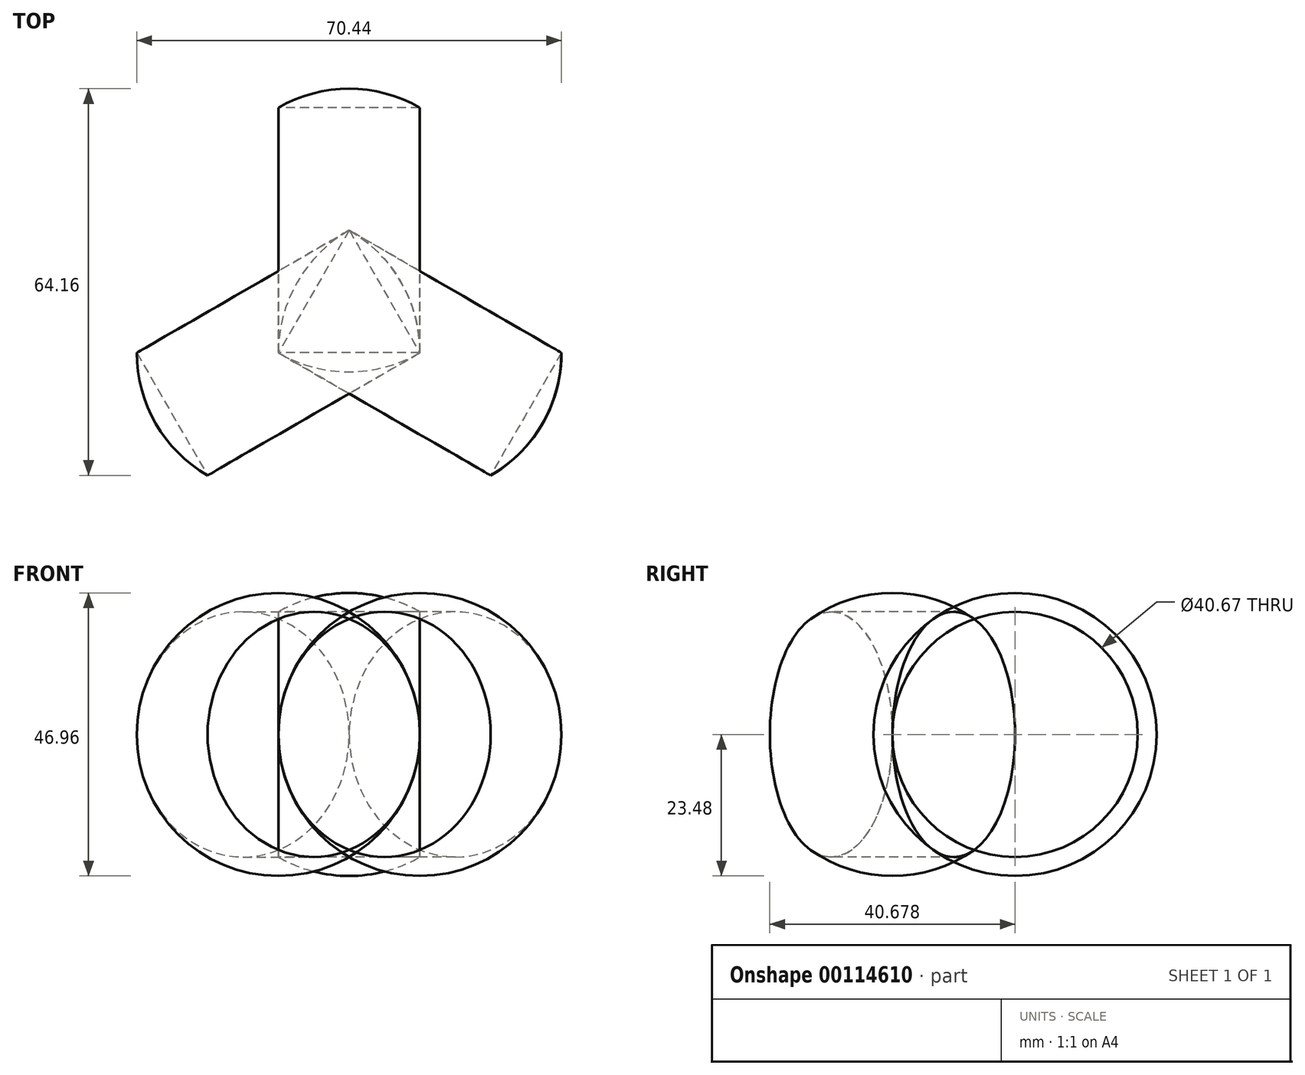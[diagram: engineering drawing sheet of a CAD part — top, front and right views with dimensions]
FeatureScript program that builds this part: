
annotation { "Feature Type Name" : "Feature", "Feature Type Description" : "" }
export const myFeature = defineFeature(function(context is Context, id is Id, definition is map)
    precondition{}
    {
        {
            var Q0;
            Q0=qCreatedBy(makeId("Top.planeOp"),FACE);
            var sketch = newSketch(context, id + "F0", { "sketchPlane" : qUnion([Q0])});
            skLineSegment(sketch, "E0", {"start": v(0, 13.56) * mm, "end": v(-11.74, -6.78) * mm});
            skLineSegment(sketch, "E1", {"start": v(-11.74, -6.78) * mm, "end": v(11.74, -6.78) * mm});
            skLineSegment(sketch, "E2", {"start": v(11.74, -6.78) * mm, "end": v(0, 13.56) * mm});
            skLineSegment(sketch, "E3", {"start": v(-11.74, -6.78) * mm, "end": v(5.87, 3.39) * mm, "construction": true});
            skLineSegment(sketch, "E4", {"start": v(-5.87, 3.39) * mm, "end": v(11.74, -6.78) * mm, "construction": true});
            skArc(sketch, "E5", {"start": v(-23.48, 13.56) * mm, "mid": v(-32.08, -18.52) * mm, "end": v(0, -27.12) * mm});
            skArc(sketch, "E6", {"start": v(0, 13.56) * mm, "mid": v(-8.6, 4.96) * mm, "end": v(-11.74, -6.78) * mm});
            skArc(sketch, "E7", {"start": v(-11.74, -6.78) * mm, "mid": v(0, -9.93) * mm, "end": v(11.74, -6.78) * mm});
            skArc(sketch, "E8.trimOffspring", {"start": v(11.74, -6.78) * mm, "mid": v(8.6, 4.96) * mm, "end": v(0, 13.56) * mm});
            skArc(sketch, "E9.trimOffspring", {"start": v(0, -27.12) * mm, "mid": v(32.08, -18.52) * mm, "end": v(23.48, 13.56) * mm});
            skArc(sketch, "E10.trimOffspring", {"start": v(23.48, 13.56) * mm, "mid": v(0, 37.04) * mm, "end": v(-23.48, 13.56) * mm});
            skLineSegment(sketch, "E11", {"start": v(-12.12, 13.56) * mm, "end": v(10.87, 13.56) * mm, "construction": true});
            skLineSegment(sketch, "E12", {"start": v(-11.74, -6.78) * mm, "end": v(-18.52, 4.96) * mm, "construction": true});
            skPoint(sketch, "E12.endSnap0", {"position": v(-8.6, 4.96) * mm});
            skLineSegment(sketch, "E13", {"start": v(11.74, -6.78) * mm, "end": v(19, 5.78) * mm, "construction": true});
            skSolve(sketch);
        }
        {
            var Q0;
            Q0=makeQuery(id+"F0.imprint","IMPRINT",FACE,{"disambiguationData":[TD([[makeQuery(id+"F0.imprint","IMPRINT",EDGE,{"derivedFrom":sQuery(id+"F0.wireOp",EDGE,"E1")}),-1.0]])]});
            var Q1;
            Q1=sQuery(id+"F0.wireOp",EDGE,"E11");
            revolve(context, id + "F1", {"entities" : qUnion([Q0]), "axis" : qUnion([Q1]), "revolveType" : RevolveType.FULL});
        }
        {
            var Q0;
            Q0=makeQuery(id+"F0.imprint","IMPRINT",FACE,{"disambiguationData":[TD([[makeQuery(id+"F0.imprint","IMPRINT",EDGE,{"derivedFrom":sQuery(id+"F0.wireOp",EDGE,"E0")}),-1.0]])]});
            var Q1;
            Q1=sQuery(id+"F0.wireOp",EDGE,"E13");
            revolve(context, id + "F2", {"entities" : qUnion([Q0]), "axis" : qUnion([Q1]), "revolveType" : RevolveType.FULL});
        }
        {
            var Q0;
            Q0=makeQuery(id+"F0.imprint","IMPRINT",FACE,{"disambiguationData":[TD([[makeQuery(id+"F0.imprint","IMPRINT",EDGE,{"derivedFrom":sQuery(id+"F0.wireOp",EDGE,"E2")}),-1.0]])]});
            var Q1;
            Q1=sQuery(id+"F0.wireOp",EDGE,"E12");
            revolve(context, id + "F3", {"entities" : qUnion([Q0]), "axis" : qUnion([Q1]), "revolveType" : RevolveType.FULL});
        }
    });
